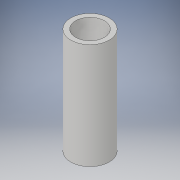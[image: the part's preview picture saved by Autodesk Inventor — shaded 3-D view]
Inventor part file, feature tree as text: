
AUTODESK INVENTOR PART (.ipt)
format: ipt  version: 2019.4 (Build 234330000, 330)  size: 96,256 bytes
history: native  units: mm
features: extrude x1, sketch x1
ambient origin geometry x8: Origin, YZ Plane, XZ Plane, XY Plane, X Axis, Y Axis, Z Axis, Center Point
bodies: Solid1 (feature_tree)
feature tree (2):
  extrude  "Extrusion1"  Depth=11.0mm
  sketch  "Sketch1"  dims[d0=3.0mm d1=4.0mm d2=11.0mm d3=0.0mm]
